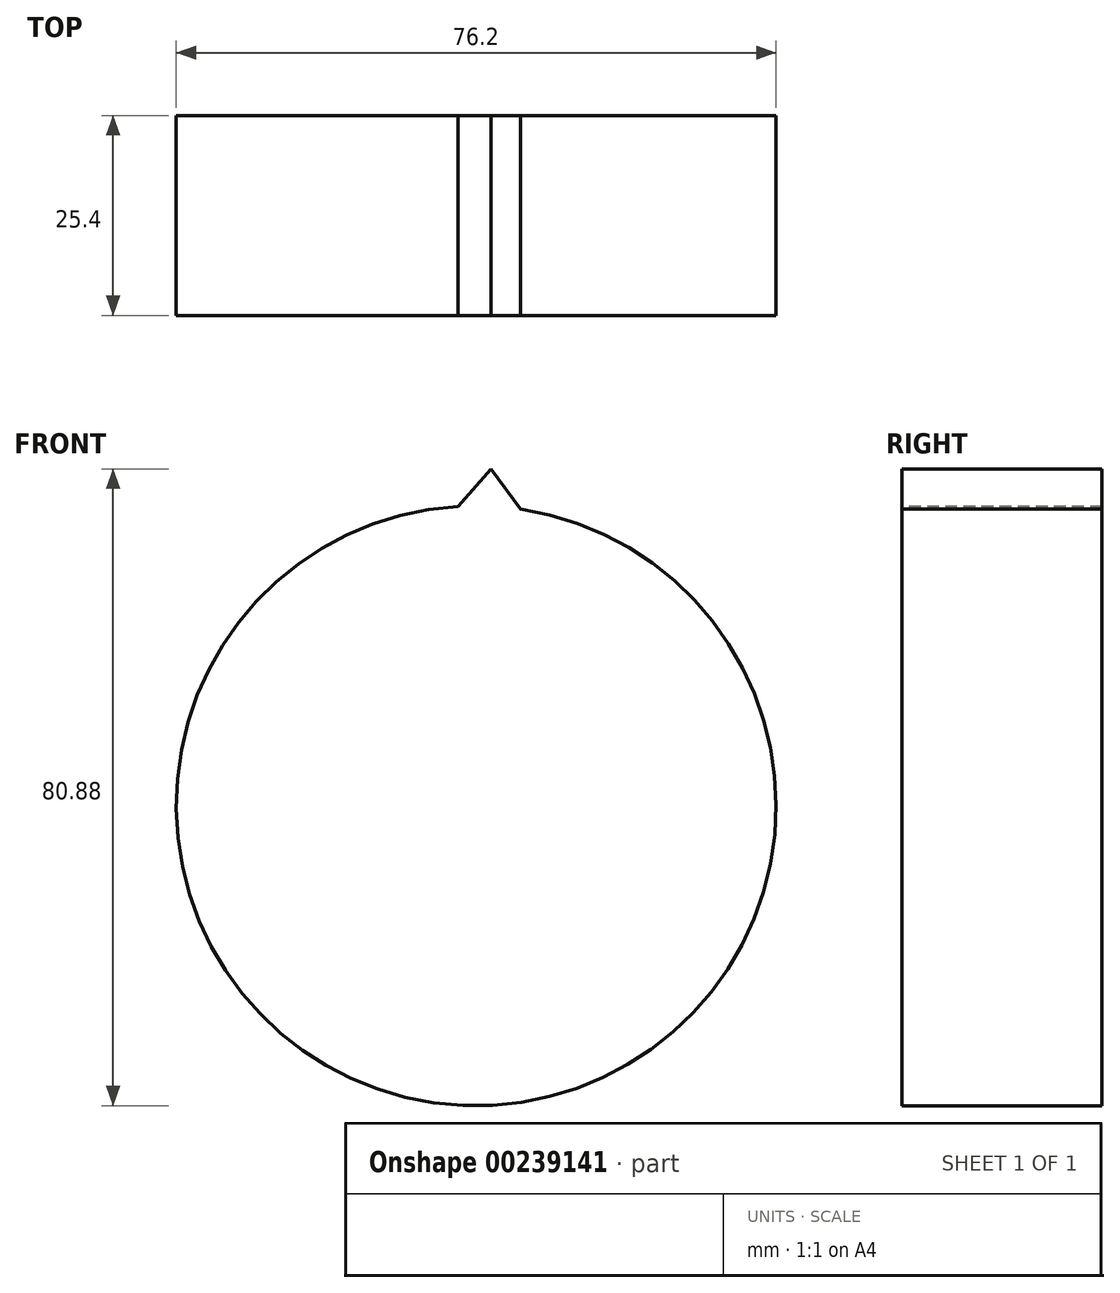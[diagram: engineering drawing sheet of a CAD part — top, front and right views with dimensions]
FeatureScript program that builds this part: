
annotation { "Feature Type Name" : "Feature", "Feature Type Description" : "" }
export const myFeature = defineFeature(function(context is Context, id is Id, definition is map)
    precondition{}
    {
        {
            var Q0;
            Q0=qCreatedBy(makeId("Front.planeOp"),FACE);
            var sketch = newSketch(context, id + "F0", { "sketchPlane" : qUnion([Q0])});
            skCircle(sketch, "E0", {"center": v(0, 0) * mm, "radius": 38.1 * mm});
            skSolve(sketch);
        }
        {
            var Q0;
            Q0 = qSketchRegion(id + "F0", true);
            extrude(context, id + "F1", {"entities" : qUnion([Q0]), "depth" : 25.4 * mm});
        }
        {
            var Q0;
            Q0=makeQuery(id+"F1.opExtrude","CAP_FACE",FACE,{"disambiguationData":[OSD([sQuery(id+"F0.wireOp",EDGE,"E0")])],"isStart":false});
            var sketch = newSketch(context, id + "F2", { "sketchPlane" : qUnion([Q0])});
            skLineSegment(sketch, "E1", {"start": v(-2.32, 38.03) * mm, "end": v(1.87, 42.78) * mm});
            skLineSegment(sketch, "E2", {"start": v(1.87, 42.78) * mm, "end": v(5.63, 37.68) * mm});
            skLineSegment(sketch, "E3", {"start": v(0, 0) * mm, "end": v(-2.32, 38.03) * mm, "construction": true});
            skLineSegment(sketch, "E4", {"start": v(0, 0) * mm, "end": v(5.63, 37.68) * mm, "construction": true});
            skArc(sketch, "E5.0", {"start": v(5.63, 37.68) * mm, "mid": v(1.66, 38.06) * mm, "end": v(-2.32, 38.03) * mm});
            skSolve(sketch);
        }
        {
            var Q0;
            Q0 = qSketchRegion(id + "F2", true);
            extrude(context, id + "F3", {"entities" : qUnion([Q0]), "operationType" : NewBodyOperationType.ADD, "oppositeDirection" : true, "depth" : 25.4 * mm});
        }
    });
